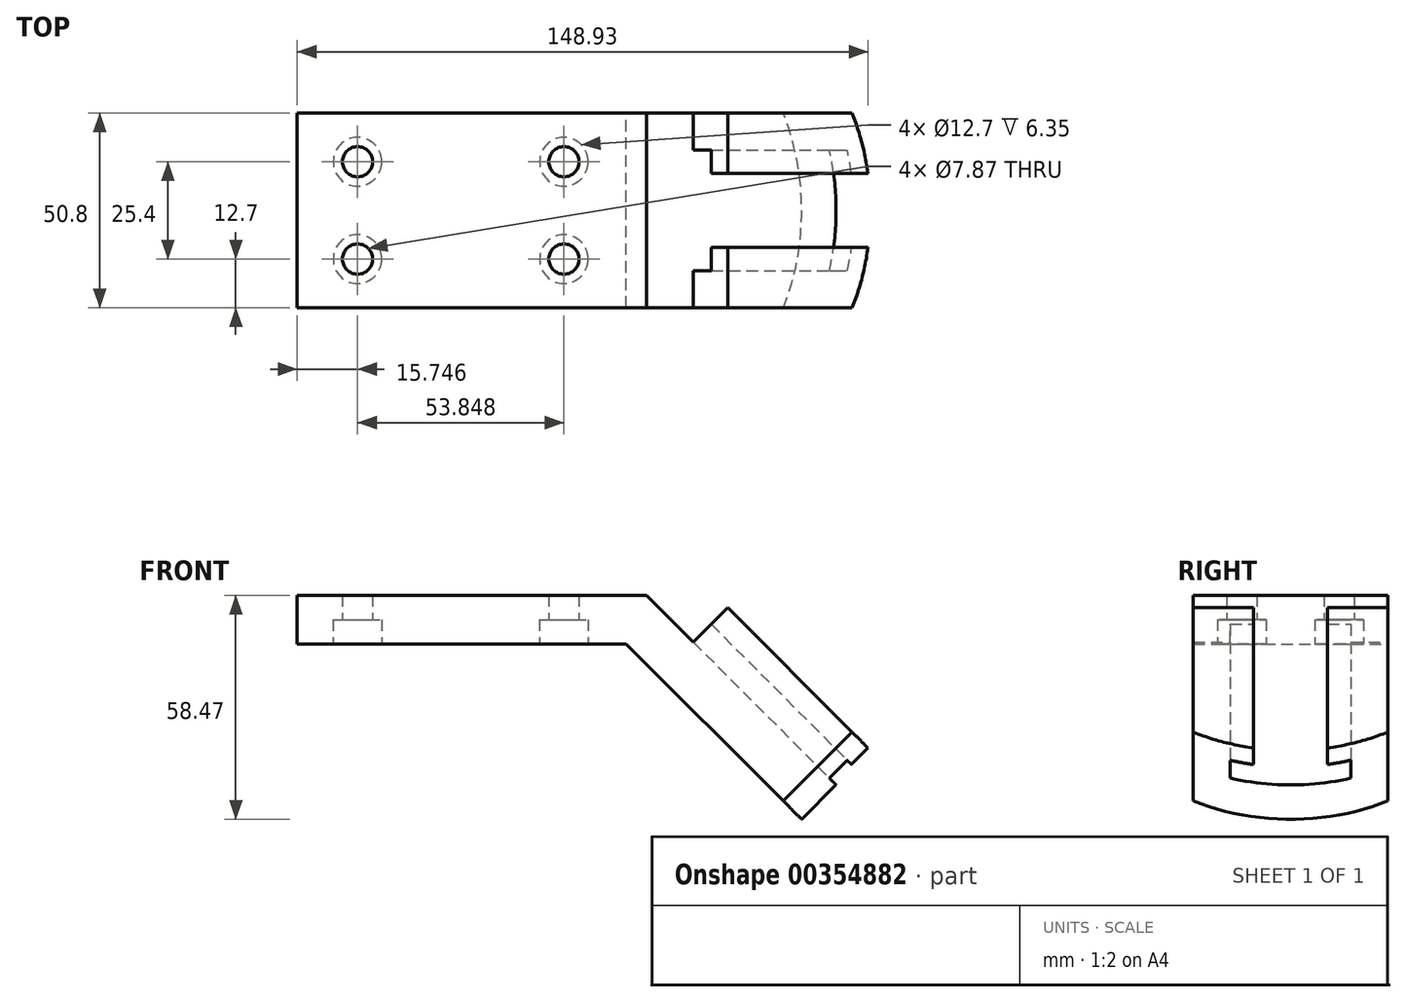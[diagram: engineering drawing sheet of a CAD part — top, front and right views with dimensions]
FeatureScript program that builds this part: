
annotation { "Feature Type Name" : "Feature", "Feature Type Description" : "" }
export const myFeature = defineFeature(function(context is Context, id is Id, definition is map)
    precondition{}
    {
        {
            var Q0;
            Q0=qCreatedBy(makeId("Front.planeOp"),FACE);
            var sketch = newSketch(context, id + "F0", { "sketchPlane" : qUnion([Q0])});
            skLineSegment(sketch, "E0", {"start": v(-85.85, 0) * mm, "end": v(-85.85, 12.7) * mm});
            skLineSegment(sketch, "E1", {"start": v(0, 0) * mm, "end": v(-85.85, 0) * mm});
            skLineSegment(sketch, "E2", {"start": v(-85.85, 12.7) * mm, "end": v(5.26, 12.7) * mm});
            skLineSegment(sketch, "E3", {"start": v(5.26, 12.7) * mm, "end": v(54.83, -36.87) * mm});
            skLineSegment(sketch, "E4", {"start": v(54.83, -36.87) * mm, "end": v(45.85, -45.85) * mm});
            skLineSegment(sketch, "E5", {"start": v(0, 0) * mm, "end": v(45.85, -45.85) * mm});
            skLineSegment(sketch, "E6", {"start": v(54.83, -36.87) * mm, "end": v(63.81, -27.9) * mm});
            skLineSegment(sketch, "E7", {"start": v(63.81, -27.9) * mm, "end": v(26.5, 9.42) * mm});
            skLineSegment(sketch, "E8", {"start": v(26.5, 9.42) * mm, "end": v(17.52, 0.44) * mm});
            skSolve(sketch);
        }
        {
            var Q0;
            Q0 = qSketchRegion(id + "F0", true);
            extrude(context, id + "F1", {"entities" : qUnion([Q0]), "endBound" : BoundingType.SYMMETRIC, "depth" : 50.8 * mm});
        }
        {
            var Q0;
            Q0=makeQuery(id+"F1.opExtrude","SWEPT_FACE",FACE,{"disambiguationData":[OSD([sQuery(id+"F0.wireOp",EDGE,"E1")])]});
            var sketch = newSketch(context, id + "F2", { "sketchPlane" : qUnion([Q0])});
            skCircle(sketch, "E9", {"center": v(-70.1, 12.7) * mm, "radius": 6.35 * mm});
            skCircle(sketch, "E10", {"center": v(-16.26, 12.7) * mm, "radius": 6.35 * mm});
            skCircle(sketch, "E11", {"center": v(-16.26, -12.7) * mm, "radius": 6.35 * mm});
            skCircle(sketch, "E12", {"center": v(-70.1, -12.7) * mm, "radius": 6.35 * mm});
            skSolve(sketch);
        }
        {
            var Q0;
            Q0=makeQuery(id+"F2.imprint","IMPRINT",FACE,{"disambiguationData":[TD([[makeQuery(id+"F2.imprint","IMPRINT",EDGE,{"derivedFrom":sQuery(id+"F2.wireOp",EDGE,"E9")}),1.0]])]});
            var Q1;
            Q1=makeQuery(id+"F2.imprint","IMPRINT",FACE,{"disambiguationData":[TD([[makeQuery(id+"F2.imprint","IMPRINT",EDGE,{"derivedFrom":sQuery(id+"F2.wireOp",EDGE,"E10")}),1.0]])]});
            var Q2;
            Q2=makeQuery(id+"F2.imprint","IMPRINT",FACE,{"disambiguationData":[TD([[makeQuery(id+"F2.imprint","IMPRINT",EDGE,{"derivedFrom":sQuery(id+"F2.wireOp",EDGE,"E11")}),1.0]])]});
            var Q3;
            Q3=makeQuery(id+"F2.imprint","IMPRINT",FACE,{"disambiguationData":[TD([[makeQuery(id+"F2.imprint","IMPRINT",EDGE,{"derivedFrom":sQuery(id+"F2.wireOp",EDGE,"E12")}),1.0]])]});
            extrude(context, id + "F3", {"entities" : qUnion([Q0, Q1, Q2, Q3]), "operationType" : NewBodyOperationType.REMOVE, "oppositeDirection" : true, "depth" : 6.35 * mm});
        }
        {
            var Q0;
            Q0=makeQuery(id+"F2.imprint","IMPRINT",FACE,{"disambiguationData":[TD([[makeQuery(id+"F2.imprint","IMPRINT",EDGE,{"derivedFrom":sQuery(id+"F2.wireOp",EDGE,"E9")}),-1.0]])]});
            var sketch = newSketch(context, id + "F4", { "sketchPlane" : qUnion([Q0])});
            skCircle(sketch, "E13", {"center": v(-16.26, -12.7) * mm, "radius": 3.94 * mm});
            skCircle(sketch, "E14", {"center": v(-16.26, 12.7) * mm, "radius": 3.94 * mm});
            skCircle(sketch, "E15", {"center": v(-70.1, 12.7) * mm, "radius": 3.94 * mm});
            skCircle(sketch, "E16", {"center": v(-70.1, -12.7) * mm, "radius": 3.94 * mm});
            skSolve(sketch);
        }
        {
            var Q0;
            Q0 = qSketchRegion(id + "F4", true);
            extrude(context, id + "F5", {"entities" : qUnion([Q0]), "operationType" : NewBodyOperationType.REMOVE, "oppositeDirection" : true, "depth" : 25.4 * mm});
        }
        {
            var Q0;
            Q0=makeQuery(id+"F1.opExtrude","SWEPT_FACE",FACE,{"disambiguationData":[OSD([sQuery(id+"F0.wireOp",EDGE,"E4"),sQuery(id+"F0.wireOp",EDGE,"E6")])]});
            var sketch = newSketch(context, id + "F6", { "sketchPlane" : qUnion([Q0])});
            skLineSegment(sketch, "E17", {"start": v(-9.65, 25.4) * mm, "end": v(-9.65, 19.3) * mm});
            skLineSegment(sketch, "E18", {"start": v(-9.65, 19.3) * mm, "end": v(-15.75, 19.3) * mm});
            skLineSegment(sketch, "E19", {"start": v(-15.75, 19.3) * mm, "end": v(-15.75, 12.7) * mm});
            skLineSegment(sketch, "E20", {"start": v(-15.75, 12.7) * mm, "end": v(15.75, 12.7) * mm});
            skLineSegment(sketch, "E21", {"start": v(15.75, 12.7) * mm, "end": v(15.75, 19.3) * mm});
            skLineSegment(sketch, "E22", {"start": v(15.75, 19.3) * mm, "end": v(9.65, 19.3) * mm});
            skLineSegment(sketch, "E23", {"start": v(9.65, 19.3) * mm, "end": v(9.65, 25.4) * mm});
            skLineSegment(sketch, "E24", {"start": v(9.65, 25.4) * mm, "end": v(-9.65, 25.4) * mm});
            skSolve(sketch);
        }
        {
            var Q0;
            Q0=makeQuery(id+"F6.imprint","IMPRINT",FACE,{"disambiguationData":[TD([[makeQuery(id+"F6.imprint","IMPRINT",EDGE,{"derivedFrom":sQuery(id+"F6.wireOp",EDGE,"E17")}),1.0]])]});
            var Q1;
            Q1=makeQuery(id+"F1.opExtrude","SWEPT_FACE",FACE,{"disambiguationData":[OSD([sQuery(id+"F0.wireOp",EDGE,"E8")])]});
            extrude(context, id + "F7", {"entities" : qUnion([Q0]), "operationType" : NewBodyOperationType.REMOVE, "endBound" : BoundingType.UP_TO_SURFACE, "oppositeDirection" : true, "endBoundEntityFace" : qUnion([Q1]), "depth" : 25.4 * mm});
        }
        {
            var Q0;
            {var subQ1=sQuery(id+"F0.wireOp",EDGE,"E7");Q0=makeQuery(id+"F7.boolean.opBoolean","SPLIT",FACE,{"disambiguationData":[TD([makeQuery(id+"F7.opExtrude","SWEPT_FACE",FACE,{"disambiguationData":[OSD([sQuery(id+"F6.wireOp",EDGE,"E17")])]})])],"derivedFrom":makeQuery(id+"F1.opExtrude","SWEPT_FACE",FACE,{"disambiguationData":[OSD([subQ1])]})});}
            var sketch = newSketch(context, id + "F8", { "sketchPlane" : qUnion([Q0])});
            skArc(sketch, "E25", {"start": v(-25.4, -57.96) * mm, "mid": v(0, -64.73) * mm, "end": v(25.4, -57.9) * mm});
            skLineSegment(sketch, "E26", {"start": v(25.4, -57.9) * mm, "end": v(-25.4, -57.96) * mm});
            skLineSegment(sketch, "E27", {"start": v(-25.4, -57.96) * mm, "end": v(-25.4, -64.84) * mm});
            skLineSegment(sketch, "E28", {"start": v(25.4, -64.84) * mm, "end": v(25.4, -57.9) * mm});
            skLineSegment(sketch, "E29", {"start": v(-25.4, -64.84) * mm, "end": v(1, -64.84) * mm});
            skLineSegment(sketch, "E30", {"start": v(1, -64.84) * mm, "end": v(25.4, -64.84) * mm});
            skSolve(sketch);
        }
        {
            var Q0;
            {var subQ0=sQuery(id+"F8.wireOp",EDGE,"E27");Q0=makeQuery(id+"F8.imprint","IMPRINT",FACE,{"disambiguationData":[TD([[makeQuery(id+"F8.imprint","IMPRINT",EDGE,{"derivedFrom":subQ0}),-1.0]])]});}
            var Q1;
            {var subQ4=sQuery(id+"F8.wireOp",EDGE,"E28");Q1=makeQuery(id+"F8.imprint","IMPRINT",FACE,{"disambiguationData":[TD([[makeQuery(id+"F8.imprint","IMPRINT",EDGE,{"derivedFrom":subQ4}),1.0]])]});}
            var Q2;
            Q2=makeQuery(id+"F1.opExtrude","SWEPT_FACE",FACE,{"disambiguationData":[OSD([sQuery(id+"F0.wireOp",EDGE,"E5")])]});
            extrude(context, id + "F9", {"entities" : qUnion([Q0, Q1]), "operationType" : NewBodyOperationType.REMOVE, "endBound" : BoundingType.UP_TO_SURFACE, "oppositeDirection" : true, "endBoundEntityFace" : qUnion([Q2]), "depth" : 25.4 * mm});
        }
    });
